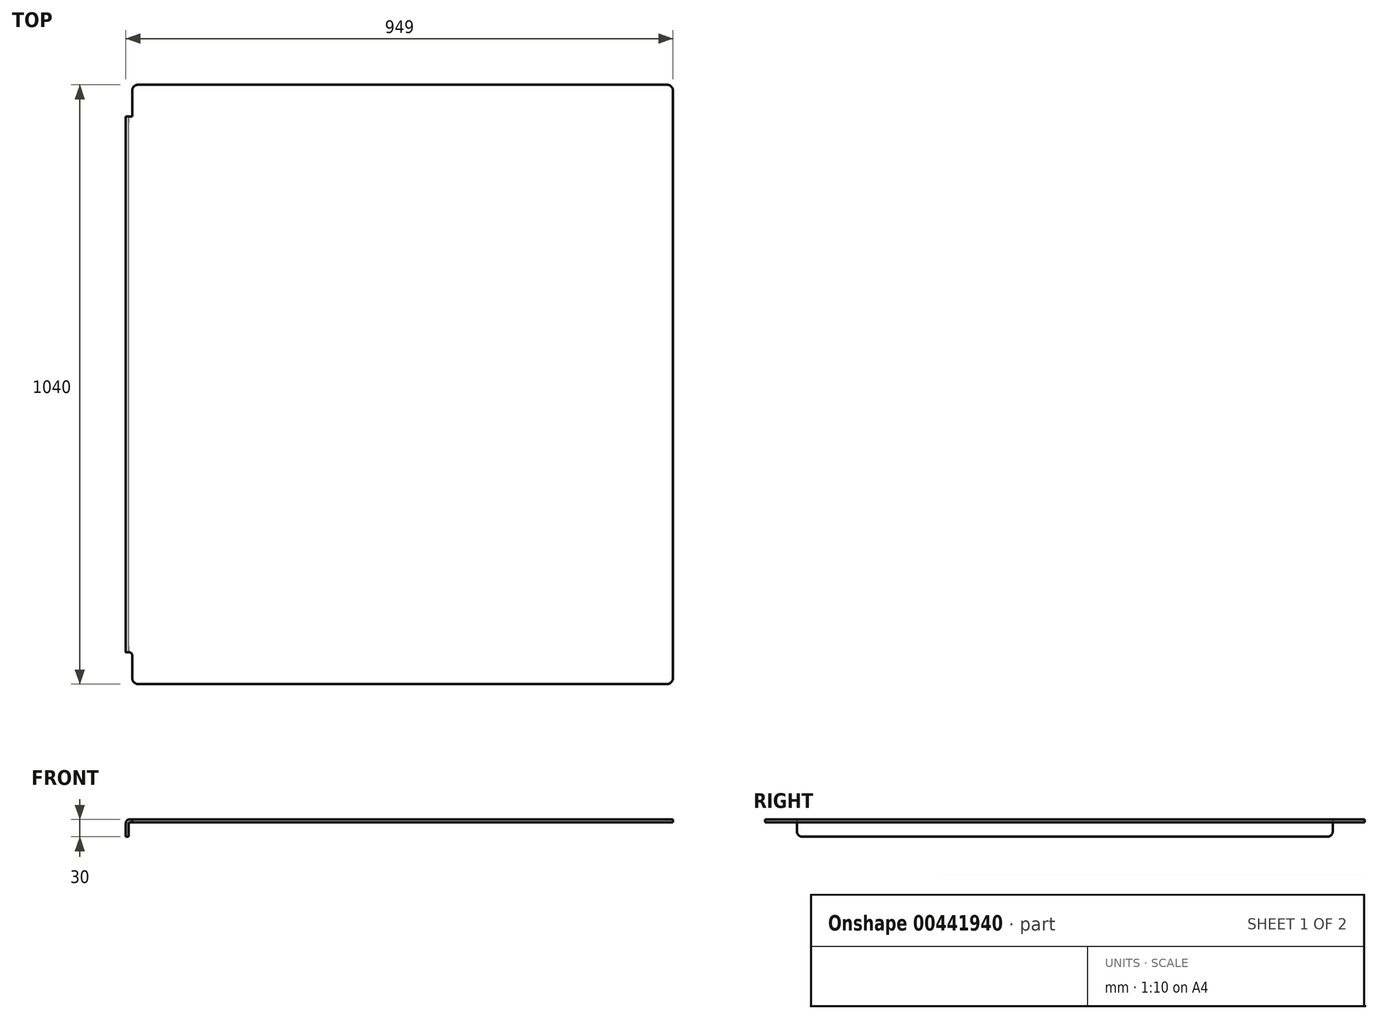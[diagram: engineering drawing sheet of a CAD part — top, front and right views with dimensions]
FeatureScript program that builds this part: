
annotation { "Feature Type Name" : "Feature", "Feature Type Description" : "" }
export const myFeature = defineFeature(function(context is Context, id is Id, definition is map)
    precondition{}
    {
        {
            var Q0;
            Q0=qCreatedBy(makeId("Top.planeOp"),FACE);
            var sketch = newSketch(context, id + "F0", { "sketchPlane" : qUnion([Q0])});
            skLineSegment(sketch, "E0.bottom", {"start": v(469, -520) * mm, "end": v(-469, -520) * mm});
            skLineSegment(sketch, "E0.top", {"start": v(469, 520) * mm, "end": v(-469, 520) * mm});
            skLineSegment(sketch, "E0.left", {"start": v(469, -520) * mm, "end": v(469, 520) * mm});
            skLineSegment(sketch, "E0.right", {"start": v(-469, -520) * mm, "end": v(-469, 520) * mm});
            skPoint(sketch, "E0.middle", {"position": v(0, 0) * mm});
            skSolve(sketch);
        }
        {
            var Q0;
            Q0 = qSketchRegion(id + "F0", true);
            extrude(context, id + "F1", {"entities" : qUnion([Q0]), "depth" : 5 * mm});
        }
        {
            var Q0;
            Q0=qCreatedBy(makeId("Front.planeOp"),FACE);
            var sketch = newSketch(context, id + "F2", { "sketchPlane" : qUnion([Q0])});
            skLineSegment(sketch, "E1.0", {"start": v(-469, 5) * mm, "end": v(-469, 0) * mm});
            skLineSegment(sketch, "E2", {"start": v(-469, 5) * mm, "end": v(-474, 5) * mm});
            skArc(sketch, "E3", {"start": v(-474, 5) * mm, "mid": v(-478.24, 3.24) * mm, "end": v(-480, -1) * mm});
            skLineSegment(sketch, "E4", {"start": v(-480, -1) * mm, "end": v(-480, -25) * mm});
            skLineSegment(sketch, "E5", {"start": v(-480, -25) * mm, "end": v(-475, -25) * mm});
            skLineSegment(sketch, "E6", {"start": v(-475, -25) * mm, "end": v(-475, -1) * mm});
            skArc(sketch, "E7", {"start": v(-474, 0) * mm, "mid": v(-474.7, -0.3) * mm, "end": v(-475, -1) * mm});
            skLineSegment(sketch, "E8", {"start": v(-474, 0) * mm, "end": v(-469, 0) * mm});
            skSolve(sketch);
        }
        {
            var Q0;
            Q0 = qSketchRegion(id + "F2", true);
            extrude(context, id + "F3", {"entities" : qUnion([Q0]), "operationType" : NewBodyOperationType.ADD, "endBound" : BoundingType.SYMMETRIC, "depth" : 930 * mm});
        }
        {
            var Q0;
            Q0=makeQuery(id+"F1.opExtrude","SWEPT_EDGE",EDGE,{"disambiguationData":[OSD([sQuery(id+"F0.wireOp",EDGE,"E0.bottom"),sQuery(id+"F0.wireOp",EDGE,"E0.right")])]});
            var Q1;
            Q1=makeQuery(id+"F3.opExtrude","CAP_EDGE",EDGE,{"disambiguationData":[OSD([sQuery(id+"F2.wireOp",EDGE,"E5")])],"isStart":false});
            var Q2;
            Q2=makeQuery(id+"F3.opExtrude","CAP_EDGE",EDGE,{"disambiguationData":[OSD([sQuery(id+"F2.wireOp",EDGE,"E5")])],"isStart":true});
            var Q3;
            Q3=makeQuery(id+"F1.opExtrude","SWEPT_EDGE",EDGE,{"disambiguationData":[OSD([sQuery(id+"F0.wireOp",EDGE,"E0.top"),sQuery(id+"F0.wireOp",EDGE,"E0.right")])]});
            var Q4;
            Q4=makeQuery(id+"F1.opExtrude","SWEPT_EDGE",EDGE,{"disambiguationData":[OSD([sQuery(id+"F0.wireOp",EDGE,"E0.top"),sQuery(id+"F0.wireOp",EDGE,"E0.left")])]});
            var Q5;
            Q5=makeQuery(id+"Ff8MlqaZz9VSBdh_1.1.F3.opExtrude","CAP_EDGE",EDGE,{"disambiguationData":[OSD([sQuery(id+"F2.wireOp",EDGE,"E5")])],"isStart":true});
            var Q6;
            Q6=makeQuery(id+"Ff8MlqaZz9VSBdh_1.1.F3.opExtrude","CAP_EDGE",EDGE,{"disambiguationData":[OSD([sQuery(id+"F2.wireOp",EDGE,"E5")])],"isStart":false});
            var Q7;
            Q7=makeQuery(id+"F1.opExtrude","SWEPT_EDGE",EDGE,{"disambiguationData":[OSD([sQuery(id+"F0.wireOp",EDGE,"E0.bottom"),sQuery(id+"F0.wireOp",EDGE,"E0.left")])]});
            fillet(context, id + "F4", {"entities" : qUnion([Q0, Q1, Q2, Q3, Q4, Q5, Q6, Q7]), "radius" : 10 * mm, "tangentPropagation" : true, "allowEdgeOverflow" : false});
        }
        {
            var Q0;
            Q0=makeQuery(id+"Ff8MlqaZz9VSBdh_1.1.F3.opExtrude","CAP_EDGE",EDGE,{"disambiguationData":[OSD([sQuery(id+"F2.wireOp",EDGE,"E1.0")])],"isStart":true});
            var Q1;
            Q1=makeQuery(id+"Ff8MlqaZz9VSBdh_1.1.F3.opExtrude","CAP_EDGE",EDGE,{"disambiguationData":[OSD([sQuery(id+"F2.wireOp",EDGE,"E1.0")])],"isStart":false});
            var Q2;
            Q2=makeQuery(id+"F3.opExtrude","CAP_EDGE",EDGE,{"disambiguationData":[OSD([sQuery(id+"F2.wireOp",EDGE,"E1.0")])],"isStart":false});
            var Q3;
            Q3=makeQuery(id+"F3.opExtrude","CAP_EDGE",EDGE,{"disambiguationData":[OSD([sQuery(id+"F2.wireOp",EDGE,"E1.0")])],"isStart":true});
            fillet(context, id + "F5", {"entities" : qUnion([Q0, Q1, Q2, Q3]), "radius" : 5 * mm, "tangentPropagation" : true, "allowEdgeOverflow" : false});
        }
    });
